# Revit family: Hager-Univers-IP43-D349-H598-Cl.II-Fire_res.encl_30min-NoHosted-CH-fr
name_source: partatom
category: Equipement électrique
units: mm (PartAtom-declared; Revit-internal decimal feet)

## family parameters
Basée sur le plan de construction = Oui
Configuration du panneau = Deux colonnes, circuits au sein
Cote de connecteur circulaire = Utiliser le diamètre
Couper avec des vides une fois chargée = Non
Partagée = Non
Point de calcul de pièce = Non
Toujours verticalement = Oui
Type d'élément = Tableau de raccordement

## types (2) — shared parameters
Commentaires du type = Univers
EF000003 - mode de pose = EV000384 - saillie
EF000007 - couleur = EV000270 - gris
EF000040 - hauteur = 598 mm  [stored 1.96194 ft]
EF000049 - profondeur = 349 mm  [stored 1.14501 ft]
EF000116 - numéro RAL = 7035
EF000118 - avec cadre/support de montage = Non
EF000266 - nombre de rangées = 3
EF000339 - type de capot = EV004216 - porte
EF001088 - possibilité de montage en saillie = Non
EF001131 - profondeur intérieure = 240 mm  [stored 0.787402 ft]
EF001596 - matériau du boîtier/corps = EV000139 - plastique
EF001613 - maintien de fonction = EV004178 - E 30
EF003532 - convient pour utilisation à l’extérieur = Non
EF004293 - indice de protection contre les chocs (IK) = EV008784 - IK10
EF004464 - type de porte = EV002646 - unique
EF006244 - couvercle/porte transparent(e) = Non
EF006306 - avec serrure = Oui
EF007800 - adapté à un parafoudre = Non
EF008873 - courant nominal (In) = 250 A
EF009170 - épaisseur de matériau du boîtier = 70 mm  [stored 0.229659 ft]
EF009171 - épaisseur de matériau de la porte/du couvercle = 22 mm  [stored 0.0721785 ft]
EF009212 - finition du couvercle = EV000116 - fermé
EF015940 - couvercle avec décharge de pression = Non
Elévation par défaut = 1219 mm
Fabricant = Hager
HG000002 - avec porte = Oui
HG000003 - Gamme = Univers
HG000006 - Encastré = Non
HG000009 - Porte à double battant = Non
HG000010 - Portes asymétriques = Non
HG000023 - Armoire double section = Non
HG000024 - Hauteur de la section basse = 600 mm
HG000026 - Installation au sol = Non
zero-valued in all types: EF000218 - profondeur d'encastrement, HG000027 - Hauteur du socle

## per-type parameters (varying)
| type | EF000008 - largeur | EF000437 - nombre d'entrées de conduit | EF002950 - largeur en nombre de modules | EF004427 - nombre de modules | EF005474 - indice de protection (IP) | EF009554 - nombre d'ouvertures pour plaques à bride | HG000004 - Référence fabricant |
| saillie IP43 L398 H598 P349  - FB31LE | 398 mm  [stored 1.30577 ft] | 1 | 12 | 36 | EV006610 - IP43 | 2 | FB31LE |
| saillie IP44 L648 H598 P349  - FB32LE | 648 mm  [stored 2.12598 ft] | 2 | 24 | 72 | EV006418 - IP44 | 4 | FB32LE |

note: [stored X ft] marks values corroborated as IEEE doubles in the binary element streams (Revit-internal decimal feet)

## geometry (parser evidence)
native form markers: Blend x4, Sweep x5
no freeform markers — native parametric forms only
